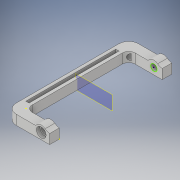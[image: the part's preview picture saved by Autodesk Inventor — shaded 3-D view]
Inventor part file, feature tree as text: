
AUTODESK INVENTOR PART (.ipt)
format: ipt  version: 2018 (Build 220112000, 112)  size: 413,184 bytes
history: native  units: in
note: dims shown in document units (in); Inventor stores cm internally (conversion verified against a paired STEP export)
features: sketch x19, extrude x11, fillet x6, hole x3, plane x1, mirror x1
ambient origin geometry x8: Origin, YZ Plane, XZ Plane, XY Plane, X Axis, Y Axis, Z Axis, Center Point
bodies: Solid1 (feature_tree)
feature tree (41):
  extrude  "Extrusion1"  Depth=0.375in
  sketch  "Sketch2"  dims[d3=0.375in d4=0.5in d5=0.375in d6=0.0in]
  extrude  "Extrusion2"  Depth=0.375in
  fillet  "Fillet1"  Radius=0.375in
  extrude  "Extrusion3"  Depth=0.375in
  extrude  "Extrusion4"  Depth=0.25in
  plane  "Work Plane1"
  mirror  "Mirror1"
  fillet  "Fillet2"  Radius=0.24in
  extrude  "Extrusion5"  Depth=0.375in
  sketch  "Sketch6"  dims[d17=1.0in d18=0.0in d19=0.24in d20=0.0in]
  extrude  "Extrusion6"  Depth=0.24in TaperAngle=0.0deg
  extrude  "Extrusion7"  Depth=0.375in
  fillet  "Fillet3"  Radius=0.25in
  fillet  "Fillet4"  Radius=0.375in
  fillet  "Fillet5"  Radius=0.25in
  fillet  "Fillet6"  Radius=0.125in
  sketch  "Sketch9"  dims[d30=0.125in d31=0.125in]
  extrude  "Extrusion8"  Depth=0.035in
  sketch  "Sketch11"  dims[d35=0.2in]
  sketch  "Sketch12"  dims[d36=0.2in d37=0.75in d38=0.375in d39=0.25in d40=0.5635in d41=0.35in d42=0.0in]
  hole  "Hole1"  [1 undecoded]
  hole  "Hole2"  [1 undecoded]
  sketch  "Sketch14"  dims[d51=3.5in d52=0.375in d53=0.0in]
  extrude  "Extrusion9"  Depth=0.125in
  extrude  "Extrusion10"  Depth=0.375in TaperAngle=0.0deg
  sketch  "Sketch17"  dims[d60=0.25in]
  extrude  "Extrusion11"  Depth=0.25in
  hole  "Hole3"  [1 undecoded]
  sketch  "Sketch1"  dims[d0=1.3in d1=0.375in]
  sketch  "Sketch3"  dims[d7=0.375in d8=0.0in d9=0.375in]
  sketch  "Sketch4"  dims[d10=0.24in d11=0.0in d12=0.25in d13=0.24in d14=0.0in]
  sketch  "Sketch5"  dims[d15=2.0in d16=0.375in]
  sketch  "Sketch7"  dims[d21=0.375in d22=0.0in d23=0.375in d24=0.25in d25=0.375in d26=0.25in d27=0.125in]
  sketch  "Sketch8"  dims[d28=0.035in d29=0.035in]
  sketch  "Sketch10"  dims[d32=4.375in d33=0.0in d34=0.2in]
  sketch  "Sketch13"  dims[d43=0.2in d44=0.75in d45=0.375in d46=0.25in d47=0.5635in d48=0.35in d49=0.0in d50=0.125in]
  sketch  "Sketch15"  dims[d54=1.0in d55=0.0in d56=0.25in]
  sketch  "Sketch16"  dims[d57=0.25in d58=0.5in d59=0.0in]
  sketch  "Sketch18"  dims[d61=0.25in d62=0.75in d63=0.375in d64=0.25in d65=0.5635in d66=0.5in d67=0.0in]
  sketch  "Sketch19"
note: 3 required parameter values undecoded (feature->parameter linkage not recoverable at this tier; creation-order binding heuristic only, values carry confidence <= 0.55)
